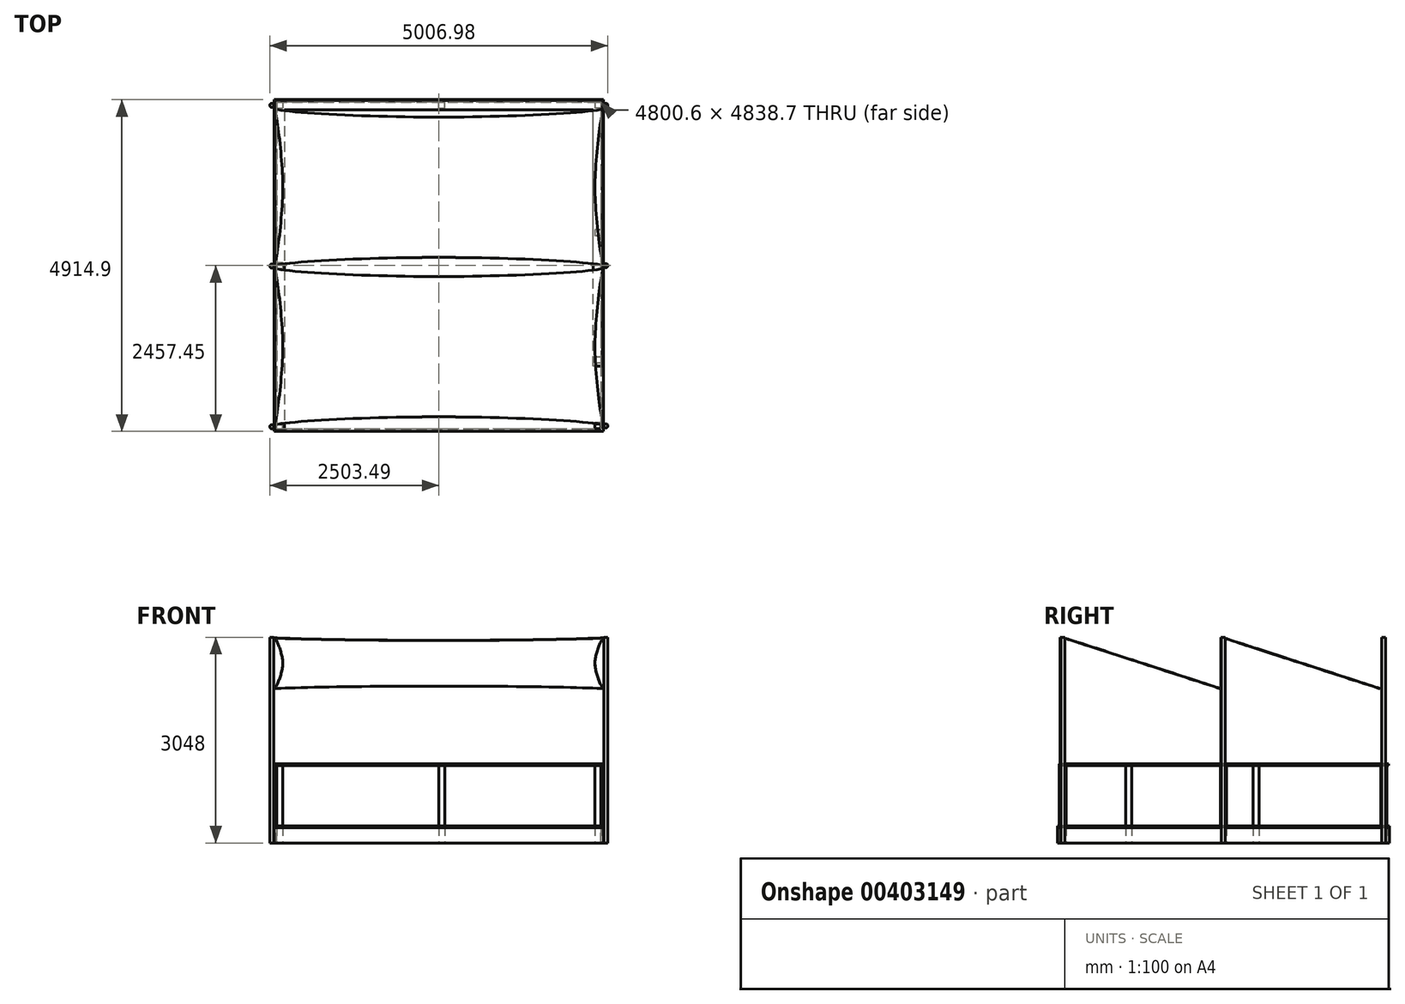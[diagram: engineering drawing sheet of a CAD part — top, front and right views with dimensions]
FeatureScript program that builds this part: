
annotation { "Feature Type Name" : "Feature", "Feature Type Description" : "" }
export const myFeature = defineFeature(function(context is Context, id is Id, definition is map)
    precondition{}
    {
        {
            var Q0;
            Q0=qCreatedBy(makeId("Top.planeOp"),FACE);
            var sketch = newSketch(context, id + "F0", { "sketchPlane" : qUnion([Q0])});
            skLineSegment(sketch, "E0.bottom", {"start": v(-2438.4, 2457.45) * mm, "end": v(2438.4, 2457.45) * mm});
            skLineSegment(sketch, "E0.top", {"start": v(-2438.4, -2457.45) * mm, "end": v(2438.4, -2457.45) * mm});
            skLineSegment(sketch, "E0.left", {"start": v(-2438.4, 2457.45) * mm, "end": v(-2438.4, -2457.45) * mm});
            skLineSegment(sketch, "E0.right", {"start": v(2438.4, 2457.45) * mm, "end": v(2438.4, -2457.45) * mm});
            skLineSegment(sketch, "E1", {"start": v(-2438.4, 2457.45) * mm, "end": v(2438.4, -2457.45) * mm, "construction": true});
            skPoint(sketch, "E2", {"position": v(0, 0) * mm});
            skSolve(sketch);
        }
        {
            var Q0;
            Q0 = qSketchRegion(id + "F0", true);
            extrude(context, id + "F1", {"entities" : qUnion([Q0]), "oppositeDirection" : true, "depth" : 25.4 * mm, "offsetDistance" : 25.4 * mm});
        }
        {
            var Q0;
            Q0=makeQuery(id+"F1.opExtrude","CAP_FACE",FACE,{"disambiguationData":[OSD([sQuery(id+"F0.wireOp",EDGE,"E0.bottom"),sQuery(id+"F0.wireOp",EDGE,"E0.top"),sQuery(id+"F0.wireOp",EDGE,"E0.left"),sQuery(id+"F0.wireOp",EDGE,"E0.right")])],"isStart":false});
            var sketch = newSketch(context, id + "F2", { "sketchPlane" : qUnion([Q0])});
            skLineSegment(sketch, "E3.0", {"start": v(-2438.4, 2457.45) * mm, "end": v(2438.4, 2457.45) * mm});
            skLineSegment(sketch, "E4.0", {"start": v(-2438.4, -2457.45) * mm, "end": v(-2438.4, 2457.45) * mm});
            skLineSegment(sketch, "E4.1", {"start": v(-2438.4, -2457.45) * mm, "end": v(2438.4, -2457.45) * mm});
            skLineSegment(sketch, "E4.2", {"start": v(2438.4, -2457.45) * mm, "end": v(2438.4, 2457.45) * mm});
            skLineSegment(sketch, "E5.0", {"start": v(-2400.3, 2419.35) * mm, "end": v(2400.3, 2419.35) * mm});
            skLineSegment(sketch, "E5.1", {"start": v(-2400.3, -2419.35) * mm, "end": v(-2400.3, 2419.35) * mm});
            skLineSegment(sketch, "E5.2", {"start": v(-2400.3, -2419.35) * mm, "end": v(2400.3, -2419.35) * mm});
            skLineSegment(sketch, "E5.3", {"start": v(2400.3, -2419.35) * mm, "end": v(2400.3, 2419.35) * mm});
            skSolve(sketch);
        }
        {
            var Q0;
            Q0 = qSketchRegion(id + "F2", true);
            extrude(context, id + "F3", {"entities" : qUnion([Q0]), "depth" : 228.6 * mm, "offsetDistance" : 25.4 * mm});
        }
        {
            var Q0;
            Q0=makeQuery(id+"F3.opExtrude","CAP_FACE",FACE,{"disambiguationData":[OSD([sQuery(id+"F2.wireOp",EDGE,"E3.0"),sQuery(id+"F2.wireOp",EDGE,"E4.0"),sQuery(id+"F2.wireOp",EDGE,"E4.1"),sQuery(id+"F2.wireOp",EDGE,"E4.2"),sQuery(id+"F2.wireOp",EDGE,"E5.0"),sQuery(id+"F2.wireOp",EDGE,"E5.1"),sQuery(id+"F2.wireOp",EDGE,"E5.2"),sQuery(id+"F2.wireOp",EDGE,"E5.3")])],"isStart":false});
            var sketch = newSketch(context, id + "F4", { "sketchPlane" : qUnion([Q0])});
            skLineSegment(sketch, "E6.bottom", {"start": v(-2400.3, 2432.05) * mm, "end": v(-2311.4, 2432.05) * mm});
            skLineSegment(sketch, "E6.top", {"start": v(-2400.3, 2343.15) * mm, "end": v(-2311.4, 2343.15) * mm});
            skLineSegment(sketch, "E6.left", {"start": v(-2400.3, 2432.05) * mm, "end": v(-2400.3, 2343.15) * mm});
            skLineSegment(sketch, "E6.right", {"start": v(-2311.4, 2432.05) * mm, "end": v(-2311.4, 2343.15) * mm});
            skLineSegment(sketch, "E7.bottom", {"start": v(2400.3, 2419.35) * mm, "end": v(2311.4, 2419.35) * mm});
            skLineSegment(sketch, "E7.top", {"start": v(2400.3, 2330.45) * mm, "end": v(2311.4, 2330.45) * mm});
            skLineSegment(sketch, "E7.left", {"start": v(2400.3, 2419.35) * mm, "end": v(2400.3, 2330.45) * mm});
            skLineSegment(sketch, "E7.right", {"start": v(2311.4, 2419.35) * mm, "end": v(2311.4, 2330.45) * mm});
            skLineSegment(sketch, "E8.bottom", {"start": v(0, -2330.45) * mm, "end": v(88.9, -2330.45) * mm});
            skLineSegment(sketch, "E8.top", {"start": v(0, -2419.35) * mm, "end": v(88.9, -2419.35) * mm});
            skLineSegment(sketch, "E8.left", {"start": v(0, -2330.45) * mm, "end": v(0, -2419.35) * mm});
            skLineSegment(sketch, "E8.right", {"start": v(88.9, -2330.45) * mm, "end": v(88.9, -2419.35) * mm});
            skLineSegment(sketch, "E9.bottom", {"start": v(-2400.3, -2419.35) * mm, "end": v(-2311.4, -2419.35) * mm});
            skLineSegment(sketch, "E9.top", {"start": v(-2400.3, -2330.45) * mm, "end": v(-2311.4, -2330.45) * mm});
            skLineSegment(sketch, "E9.left", {"start": v(-2400.3, -2419.35) * mm, "end": v(-2400.3, -2330.45) * mm});
            skLineSegment(sketch, "E9.right", {"start": v(-2311.4, -2419.35) * mm, "end": v(-2311.4, -2330.45) * mm});
            skLineSegment(sketch, "E10.bottom", {"start": v(-2400.3, -44.45) * mm, "end": v(-2311.4, -44.45) * mm});
            skLineSegment(sketch, "E10.top", {"start": v(-2400.3, 44.45) * mm, "end": v(-2311.4, 44.45) * mm});
            skLineSegment(sketch, "E10.left", {"start": v(-2400.3, -44.45) * mm, "end": v(-2400.3, 44.45) * mm});
            skLineSegment(sketch, "E10.right", {"start": v(-2311.4, -44.45) * mm, "end": v(-2311.4, 44.45) * mm});
            skLineSegment(sketch, "E11.bottom", {"start": v(2400.3, -2419.35) * mm, "end": v(2311.4, -2419.35) * mm});
            skLineSegment(sketch, "E11.top", {"start": v(2400.3, -2330.45) * mm, "end": v(2311.4, -2330.45) * mm});
            skLineSegment(sketch, "E11.left", {"start": v(2400.3, -2419.35) * mm, "end": v(2400.3, -2330.45) * mm});
            skLineSegment(sketch, "E11.right", {"start": v(2311.4, -2419.35) * mm, "end": v(2311.4, -2330.45) * mm});
            skLineSegment(sketch, "E12.bottom", {"start": v(2400.3, -527.05) * mm, "end": v(2311.4, -527.05) * mm});
            skLineSegment(sketch, "E12.top", {"start": v(2400.3, -438.15) * mm, "end": v(2311.4, -438.15) * mm});
            skLineSegment(sketch, "E12.left", {"start": v(2400.3, -527.05) * mm, "end": v(2400.3, -438.15) * mm});
            skLineSegment(sketch, "E12.right", {"start": v(2311.4, -527.05) * mm, "end": v(2311.4, -438.15) * mm});
            skLineSegment(sketch, "E13.bottom", {"start": v(2400.3, 1358.9) * mm, "end": v(2311.4, 1358.9) * mm});
            skLineSegment(sketch, "E13.top", {"start": v(2400.3, 1447.8) * mm, "end": v(2311.4, 1447.8) * mm});
            skLineSegment(sketch, "E13.left", {"start": v(2400.3, 1358.9) * mm, "end": v(2400.3, 1447.8) * mm});
            skLineSegment(sketch, "E13.right", {"start": v(2311.4, 1358.9) * mm, "end": v(2311.4, 1447.8) * mm});
            skSolve(sketch);
        }
        {
            var Q0;
            Q0 = qSketchRegion(id + "F4", true);
            extrude(context, id + "F5", {"entities" : qUnion([Q0]), "oppositeDirection" : true, "depth" : 1149.35 * mm, "offsetDistance" : 25.4 * mm});
        }
        {
            var Q0;
            Q0=makeQuery(id+"F5.opExtrude","CAP_FACE",FACE,{"disambiguationData":[OSD([sQuery(id+"F4.wireOp",EDGE,"E6.bottom"),sQuery(id+"F4.wireOp",EDGE,"E6.top"),sQuery(id+"F4.wireOp",EDGE,"E6.left"),sQuery(id+"F4.wireOp",EDGE,"E6.right")])],"isStart":false});
            var sketch = newSketch(context, id + "F6", { "sketchPlane" : qUnion([Q0])});
            skLineSegment(sketch, "E14", {"start": v(-2286, -2432.05) * mm, "end": v(-2425.7, -2432.05) * mm});
            skLineSegment(sketch, "E15", {"start": v(-2425.7, -2432.05) * mm, "end": v(-2425.7, 2444.75) * mm});
            skLineSegment(sketch, "E16", {"start": v(-2425.7, 2444.75) * mm, "end": v(2425.7, 2444.75) * mm});
            skLineSegment(sketch, "E17", {"start": v(2425.7, 2444.75) * mm, "end": v(2425.7, -1492.25) * mm});
            skLineSegment(sketch, "E18", {"start": v(2425.7, -1492.25) * mm, "end": v(2286, -1492.25) * mm});
            skLineSegment(sketch, "E19", {"start": v(2286, -1492.25) * mm, "end": v(2286, 2305.05) * mm});
            skLineSegment(sketch, "E20", {"start": v(2286, 2305.05) * mm, "end": v(-2286, 2305.05) * mm});
            skLineSegment(sketch, "E21", {"start": v(-2286, 2305.05) * mm, "end": v(-2286, -2432.05) * mm});
            skLineSegment(sketch, "E22", {"start": v(0, 2305.05) * mm, "end": v(0, 2444.75) * mm, "construction": true});
            skSolve(sketch);
        }
        {
            var Q0;
            Q0 = qSketchRegion(id + "F6", true);
            extrude(context, id + "F7", {"entities" : qUnion([Q0]), "depth" : 25.4 * mm, "offsetDistance" : 25.4 * mm});
        }
        {
            var Q0;
            Q0=makeQuery(id+"F3.opExtrude","CAP_FACE",FACE,{"disambiguationData":[OSD([sQuery(id+"F2.wireOp",EDGE,"E3.0"),sQuery(id+"F2.wireOp",EDGE,"E4.0"),sQuery(id+"F2.wireOp",EDGE,"E4.1"),sQuery(id+"F2.wireOp",EDGE,"E4.2"),sQuery(id+"F2.wireOp",EDGE,"E5.0"),sQuery(id+"F2.wireOp",EDGE,"E5.1"),sQuery(id+"F2.wireOp",EDGE,"E5.2"),sQuery(id+"F2.wireOp",EDGE,"E5.3")])],"isStart":false});
            var sketch = newSketch(context, id + "F8", { "sketchPlane" : qUnion([Q0])});
            skCircle(sketch, "E23", {"center": v(-2473.32, -2374.9) * mm, "radius": 30.16 * mm});
            skCircle(sketch, "E24", {"center": v(2473.33, -2374.9) * mm, "radius": 30.16 * mm});
            skCircle(sketch, "E25", {"center": v(2473.32, 2374.9) * mm, "radius": 30.16 * mm});
            skCircle(sketch, "E26", {"center": v(-2473.32, 2387.6) * mm, "radius": 30.16 * mm});
            skCircle(sketch, "E27", {"center": v(-2473.32, 6.35) * mm, "radius": 30.16 * mm});
            skCircle(sketch, "E28", {"center": v(2473.32, 0) * mm, "radius": 30.16 * mm});
            skLineSegment(sketch, "E29.0", {"start": v(2311.4, 2419.35) * mm, "end": v(2311.4, 2330.45) * mm, "construction": true});
            skLineSegment(sketch, "E30", {"start": v(2311.4, 2374.9) * mm, "end": v(2473.32, 2374.9) * mm, "construction": true});
            skLineSegment(sketch, "E31.0", {"start": v(-2311.4, 2432.05) * mm, "end": v(-2311.4, 2343.15) * mm, "construction": true});
            skLineSegment(sketch, "E32", {"start": v(-2311.4, 2387.6) * mm, "end": v(-2473.32, 2387.6) * mm, "construction": true});
            skLineSegment(sketch, "E33.0", {"start": v(2311.4, -2419.35) * mm, "end": v(2311.4, -2330.45) * mm, "construction": true});
            skLineSegment(sketch, "E34", {"start": v(2311.4, -2374.9) * mm, "end": v(2473.32, -2374.9) * mm, "construction": true});
            skLineSegment(sketch, "E35.0", {"start": v(-2311.4, -2419.35) * mm, "end": v(-2311.4, -2330.45) * mm, "construction": true});
            skLineSegment(sketch, "E36", {"start": v(-2311.4, -2374.9) * mm, "end": v(-2473.32, -2374.9) * mm, "construction": true});
            skLineSegment(sketch, "E37", {"start": v(-2473.32, -2374.9) * mm, "end": v(-2473.32, 6.35) * mm, "construction": true});
            skLineSegment(sketch, "E38", {"start": v(-2473.32, 6.35) * mm, "end": v(-2473.32, 2387.6) * mm, "construction": true});
            skLineSegment(sketch, "E39", {"start": v(2473.32, -2374.9) * mm, "end": v(2473.32, 0) * mm, "construction": true});
            skLineSegment(sketch, "E40", {"start": v(2473.32, 0) * mm, "end": v(2473.32, 2374.9) * mm, "construction": true});
            skSolve(sketch);
        }
        {
            var Q0;
            Q0 = qSketchRegion(id + "F8", true);
            extrude(context, id + "F9", {"entities" : qUnion([Q0]), "oppositeDirection" : true, "depth" : 3048 * mm, "offsetDistance" : 25.4 * mm});
        }
        {
            var Q0;
            Q0=qCreatedBy(makeId("Right.planeOp"),FACE);
            var sketch = newSketch(context, id + "F10", { "sketchPlane" : qUnion([Q0])});
            skLineSegment(sketch, "E41", {"start": v(2319.34, 2032) * mm, "end": v(0, 2784.64) * mm});
            skLineSegment(sketch, "E42", {"start": v(0, 2032) * mm, "end": v(-2332.04, 2744.32) * mm});
            skLineSegment(sketch, "E43.0", {"start": v(2405.06, 2794) * mm, "end": v(2344.74, 2794) * mm});
            skPoint(sketch, "E44", {"position": v(2374.9, 2794) * mm});
            skLineSegment(sketch, "E45", {"start": v(2319.34, 2794) * mm, "end": v(2319.34, 2032) * mm});
            skLineSegment(sketch, "E46.0", {"start": v(-2357.44, 2794) * mm, "end": v(-2417.76, 2794) * mm});
            skLineSegment(sketch, "E47", {"start": v(-2332.04, 2794) * mm, "end": v(-2332.04, 2744.32) * mm});
            skLineSegment(sketch, "E48", {"start": v(3444.53, 2032) * mm, "end": v(1428.47, -254) * mm});
            skPoint(sketch, "E49", {"position": v(2374.9, 819.15) * mm});
            skLineSegment(sketch, "E50.0", {"start": v(2419.35, 895.35) * mm, "end": v(2330.45, 895.35) * mm});
            skLineSegment(sketch, "E51", {"start": v(2374.9, 819.15) * mm, "end": v(2374.9, 895.35) * mm});
            skLineSegment(sketch, "E52", {"start": v(552.45, -254) * mm, "end": v(-163.54, 2708.71) * mm});
            skLineSegment(sketch, "E53", {"start": v(5668.54, 2032) * mm, "end": v(-3300.71, 2032) * mm, "construction": true});
            skLineSegment(sketch, "E54", {"start": v(0, 2032) * mm, "end": v(531.84, 3668.83) * mm});
            skLineSegment(sketch, "E55", {"start": v(-348.8, 2138.54) * mm, "end": v(175.44, 3752) * mm});
            skLineSegment(sketch, "E56", {"start": v(-163.54, 2708.71) * mm, "end": v(2319.34, 2032) * mm});
            skSolve(sketch);
        }
        {
            var Q0;
            Q0=sQuery(id+"F10.wireOp",EDGE,"E41");
            var Q1;
            Q1=sQuery(id+"F10.wireOp",EDGE,"E42");
            var Q2;
            Q2=sQuery(id+"F10.wireOp",EDGE,"0hBOjXTt-NBWv-TD4D-vwle-BH83RLSWMM7G");
            extrude(context, id + "F11", {"bodyType" : ToolBodyType.SURFACE, "surfaceEntities" : qUnion([Q0, Q1, Q2]), "endBound" : BoundingType.SYMMETRIC, "depth" : 4876.8 * mm, "offsetDistance" : 25.4 * mm});
        }
        {
            var Q0;
            Q0=makeQuery(id+"F11.opExtrude","SWEPT_FACE",FACE,{"disambiguationData":[OSD([sQuery(id+"F10.wireOp",EDGE,"E41")])]});
            var sketch = newSketch(context, id + "F12", { "sketchPlane" : qUnion([Q0])});
            skLineSegment(sketch, "E57", {"start": v(2438.4, 359.69) * mm, "end": v(-2438.4, 359.69) * mm, "construction": true});
            skLineSegment(sketch, "E58", {"start": v(0, -859.51) * mm, "end": v(0, 1578.89) * mm, "construction": true});
            skFitSpline(sketch, "E59", {"points": [v(2438.4, -859.51) * mm, v(2311.4, 359.69) * mm], "startDerivative": vector(-146.06, 336.92) * mm, "endDerivative": vector(0, 1144.9) * mm});
            skFitSpline(sketch, "E60", {"points": [v(2438.4, -859.51) * mm, v(0, -732.51) * mm], "startDerivative": vector(-896.25, 219.71) * mm, "endDerivative": vector(-2779.15, 0) * mm});
            skFitSpline(sketch, "E61.MirrorCS", {"points": [v(-2438.4, -859.51) * mm, v(0, -732.51) * mm], "startDerivative": vector(896.25, 219.71) * mm, "endDerivative": vector(2779.15, 0) * mm});
            skFitSpline(sketch, "E62.MirrorCS", {"points": [v(-2438.4, -859.51) * mm, v(-2311.4, 359.69) * mm], "startDerivative": vector(146.06, 336.92) * mm, "endDerivative": vector(0, 1144.9) * mm});
            skFitSpline(sketch, "E63.MirrorCS", {"points": [v(-2438.4, 1578.89) * mm, v(-2311.4, 359.69) * mm], "startDerivative": vector(146.06, -336.92) * mm, "endDerivative": vector(0, -1144.9) * mm});
            skFitSpline(sketch, "E64.MirrorCS", {"points": [v(-2438.4, 1578.89) * mm, v(0, 1451.89) * mm], "startDerivative": vector(896.25, -219.71) * mm, "endDerivative": vector(2779.15, 0) * mm});
            skFitSpline(sketch, "E65.MirrorCS", {"points": [v(2438.4, 1578.89) * mm, v(0, 1451.89) * mm], "startDerivative": vector(-896.25, -219.71) * mm, "endDerivative": vector(-2779.15, 0) * mm});
            skFitSpline(sketch, "E66.MirrorCS", {"points": [v(2438.4, 1578.89) * mm, v(2311.4, 359.69) * mm], "startDerivative": vector(-146.06, -336.92) * mm, "endDerivative": vector(0, -1144.9) * mm});
            skSolve(sketch);
        }
        {
            var Q0;
            Q0 = qSketchRegion(id + "F12", true);
            extrude(context, id + "F13", {"entities" : qUnion([Q0]), "depth" : 3.17 * mm, "offsetDistance" : 25.4 * mm});
        }
        {
            var Q0;
            Q0=makeQuery(id+"F13.opExtrude","SWEPT_BODY",BODY,{"disambiguationData":[OSD([sQuery(id+"F12.wireOp",EDGE,"E59"),sQuery(id+"F12.wireOp",EDGE,"E60"),sQuery(id+"F12.wireOp",EDGE,"E61.MirrorCS"),sQuery(id+"F12.wireOp",EDGE,"E62.MirrorCS"),sQuery(id+"F12.wireOp",EDGE,"E63.MirrorCS"),sQuery(id+"F12.wireOp",EDGE,"E64.MirrorCS"),sQuery(id+"F12.wireOp",EDGE,"E65.MirrorCS"),sQuery(id+"F12.wireOp",EDGE,"E66.MirrorCS")])]});
            transform(context, id + "F14", {"entities" : qUnion([Q0]), "transformType" : TransformType.TRANSLATION_3D, "dx" : 0 * mm, "dy" : -2362.2 * mm, "dz" : 0 * mm, "makeCopy" : true});
        }
    });
